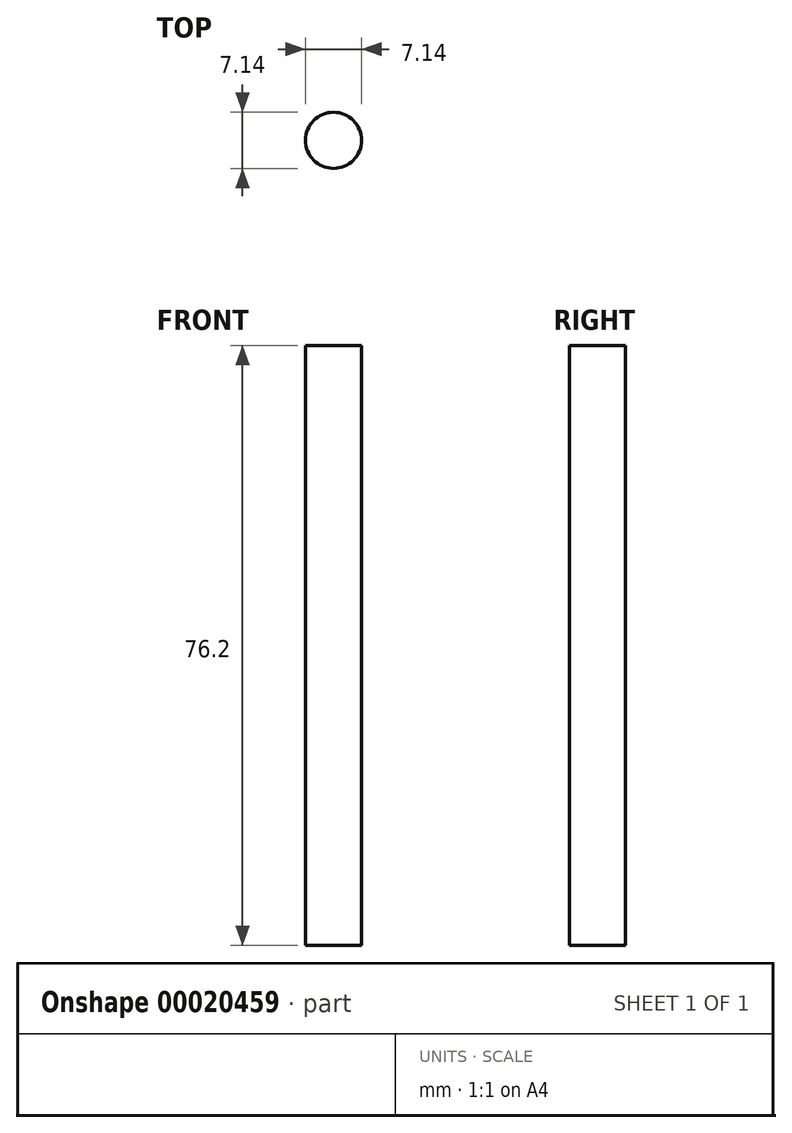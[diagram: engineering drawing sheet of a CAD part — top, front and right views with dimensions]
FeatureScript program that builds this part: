
annotation { "Feature Type Name" : "Feature", "Feature Type Description" : "" }
export const myFeature = defineFeature(function(context is Context, id is Id, definition is map)
    precondition{}
    {
        {
            var Q0;
            Q0=qCreatedBy(makeId("Right.planeOp"),FACE);
            var sketch = newSketch(context, id + "F0", { "sketchPlane" : qUnion([Q0])});
            skLineSegment(sketch, "E0.bottom", {"start": v(-51.06, 85.02) * mm, "end": v(44.2, 85.02) * mm});
            skLineSegment(sketch, "E0.top", {"start": v(-51.06, 8.82) * mm, "end": v(44.2, 8.82) * mm});
            skLineSegment(sketch, "E0.left", {"start": v(-51.06, 85.02) * mm, "end": v(-51.06, 8.82) * mm});
            skLineSegment(sketch, "E0.right", {"start": v(44.2, 85.02) * mm, "end": v(44.2, 8.82) * mm});
            skLineSegment(sketch, "E1.0", {"start": v(-3.56, 85.02) * mm, "end": v(-3.56, 8.82) * mm, "construction": true});
            skCircle(sketch, "E2", {"center": v(-3.56, 46.92) * mm, "radius": 23.75 * mm});
            skSolve(sketch);
        }
        {
            var Q0;
            Q0=makeQuery(id+"F0.imprint","IMPRINT",FACE,{"disambiguationData":[TD([[makeQuery(id+"F0.imprint","IMPRINT",EDGE,{"derivedFrom":sQuery(id+"F0.wireOp",EDGE,"E0.bottom")}),-1.0]])]});
            extrude(context, id + "F1", {"entities" : qUnion([Q0]), "depth" : 25.4 * mm});
        }
        {
            var Q0;
            Q0=makeQuery(id+"F1.opExtrude","SWEPT_FACE",FACE,{"disambiguationData":[OSD([sQuery(id+"F0.wireOp",EDGE,"E0.bottom")])]});
            var sketch = newSketch(context, id + "F2", { "sketchPlane" : qUnion([Q0])});
            skLineSegment(sketch, "E3.0", {"start": v(25.4, -41.53) * mm, "end": v(0, -41.53) * mm, "construction": true});
            skLineSegment(sketch, "E4", {"start": v(25.4, -3.43) * mm, "end": v(0, -3.43) * mm, "construction": true});
            skCircle(sketch, "E5", {"center": v(12.7, -41.53) * mm, "radius": 3.57 * mm});
            skCircle(sketch, "E6.MirrorC", {"center": v(12.7, 34.67) * mm, "radius": 3.57 * mm});
            skSolve(sketch);
        }
        {
            var Q0;
            Q0=makeQuery(id+"F2.imprint","IMPRINT",FACE,{"disambiguationData":[TD([[makeQuery(id+"F2.imprint","IMPRINT",EDGE,{"derivedFrom":sQuery(id+"F2.wireOp",EDGE,"E6.MirrorC")}),-1.0]])]});
            var Q1;
            Q1=makeQuery(id+"F2.imprint","IMPRINT",FACE,{"disambiguationData":[TD([[makeQuery(id+"F2.imprint","IMPRINT",EDGE,{"derivedFrom":sQuery(id+"F2.wireOp",EDGE,"E5")}),1.0]])]});
            var Q2;
            Q2=sQuery(id+"F2.wireOp",EDGE,"E6.MirrorC");
            var Q3;
            Q3=sQuery(id+"F2.wireOp",EDGE,"E5");
            extrude(context, id + "F3", {"entities" : qUnion([Q0, Q1]), "operationType" : NewBodyOperationType.REMOVE, "surfaceEntities" : qUnion([Q2, Q3]), "endBound" : BoundingType.THROUGH_ALL, "oppositeDirection" : true, "depth" : 25.4 * mm});
        }
    });
